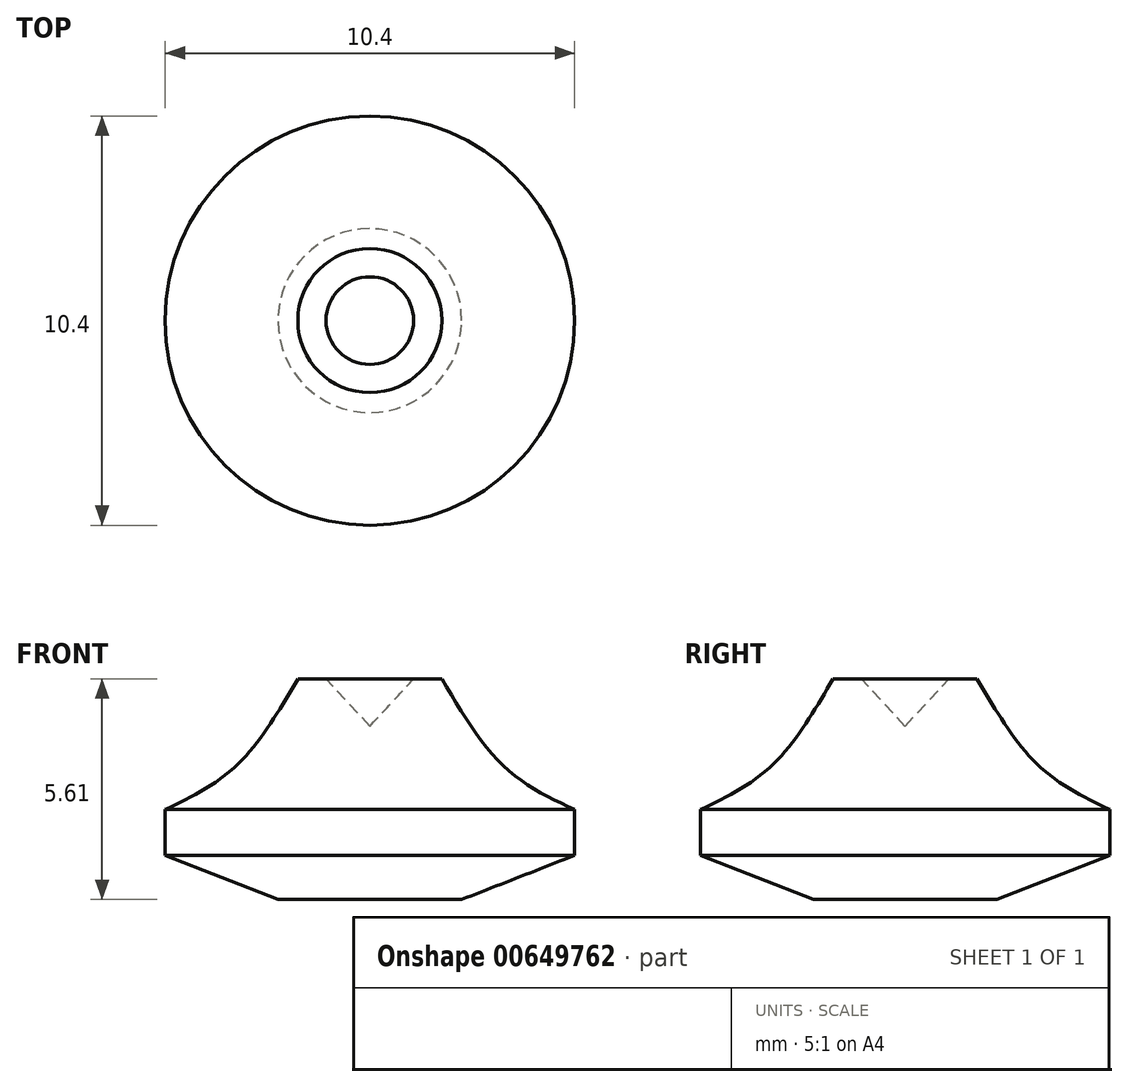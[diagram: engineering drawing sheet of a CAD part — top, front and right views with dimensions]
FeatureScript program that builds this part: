
annotation { "Feature Type Name" : "Feature", "Feature Type Description" : "" }
export const myFeature = defineFeature(function(context is Context, id is Id, definition is map)
    precondition{}
    {
        {
            var Q0;
            Q0=qCreatedBy(makeId("Front.planeOp"),FACE);
            var sketch = newSketch(context, id + "F0", { "sketchPlane" : qUnion([Q0])});
            skLineSegment(sketch, "E0", {"start": v(0, 1.78) * mm, "end": v(0, -2.62) * mm});
            skLineSegment(sketch, "E1", {"start": v(0, -2.62) * mm, "end": v(2.34, -2.62) * mm});
            skLineSegment(sketch, "E2", {"start": v(2.34, -2.62) * mm, "end": v(5.2, -1.5) * mm});
            skLineSegment(sketch, "E3", {"start": v(5.2, -1.5) * mm, "end": v(5.2, -0.33) * mm});
            skFitSpline(sketch, "E4", {"points": [v(5.2, -0.33) * mm, v(3.44, 0.73) * mm, v(1.83, 2.99) * mm], "startDerivative": vector(-4, 1.86) * mm, "endDerivative": vector(-2.78, 4.7) * mm});
            skLineSegment(sketch, "E5", {"start": v(1.83, 2.99) * mm, "end": v(1.11, 2.99) * mm});
            skLineSegment(sketch, "E6", {"start": v(1.11, 2.99) * mm, "end": v(0, 1.78) * mm});
            skSolve(sketch);
        }
        {
            var Q0;
            Q0=makeQuery(id+"F0.imprint","IMPRINT",FACE,{"disambiguationData":[TD([[makeQuery(id+"F0.imprint","IMPRINT",EDGE,{"derivedFrom":sQuery(id+"F0.wireOp",EDGE,"E0")}),1.0]])]});
            var Q1;
            Q1=sQuery(id+"F0.wireOp",EDGE,"E0");
            revolve(context, id + "F1", {"entities" : qUnion([Q0]), "axis" : qUnion([Q1]), "revolveType" : RevolveType.FULL});
        }
    });
